# Revit family: 9144944
name_source: partatom
category: Lighting Fixtures
revit_build: Autodesk Revit 2017 (Build: 20190507_1515(x64)
units: mm (PartAtom-declared; Revit-internal decimal feet)

## family parameters
Cut with Voids When Loaded = No
Host = Face
Light Source = Yes
OmniClass Number = 23.80.70.00
OmniClass Title = Lighting
Part Type = Normal
Room Calculation Point = No
Round Connector Dimension = Use Diameter
Shared = No

## types (2) — shared parameters
Apparent Load = 7 VA
Assembly Code = D5020200
AssetType = Fixed
ClassificationName = Uniclass2015
ClassificationValue = EF_70_80
Color Filter = 16777215
Default Elevation = 1219 mm
Dimming Lamp Color Temperature Shift = <None>
DimmingControlOptions = Non dimmable
DocumentationLiterature = http://www.sylvania-lighting.com
DurationUnit = hours
ElectricShockClassification = Class II
Emit Shape Visible in Rendering = No
Emit from Rectangle Length = 305 mm  [stored 1.00066 ft]
Emit from Rectangle Width = 40 mm  [stored 0.131234 ft]
ExpectedLife = 50000
IfcExportAs = IfcLightFixtureType
IfcExportType = IfcLightFixtureType
IngressProtection = IP65
InputNominalFrequency = 50/60 Hz
InputVoltage = 230-240V~
Keynote = 16500
Lamp = LED
LampColourTemperature = 4000 K
LampNominalLuminous = 135 lm
LampsType = LED
LuminousEfficacy = 46.53 lm/W
Manufacturer = Feilo Sylvania
ManufacturerName = Feilo Sylvania
Material_1_SYL = PC/ABS Plastic
Material_2_SYL = PC/ABS Plastic Transparent
Material_3_SYL = LED-Sylvania
Material_4_SYL = EM sign
Model = SYLSAFE IP65 LED M3
ModelNumber = 9144944
ModelReference = SYLSAFE IP65 LED M3
Name = SYLSAFE IP65 LED M3
NominalDepth = 110 mm  [stored 0.360892 ft]
NominalHeight = 60 mm  [stored 0.19685 ft]
NominalLength = 346 mm  [stored 1.13517 ft]
Photometric Web File = 9144944.ies
PowerConsumption = 7 W
Tilt Angle = -90.00°
Type Image = <None>
TypeName = SYLSAFE IP65 LED M3
URL = http://www.sylvania-lighting.com
Voltage = 230 V
Weight = 2.75 kg
zero-valued in all types: Cost, PowerFactor

## per-type parameters (varying)
| type | Cover_SYL | EmergencyAccessory_SYL |
| 9144944 SYLSAFE IP65 LED M3 | Yes | No |
| 9144944 SYLSAFE IP65 LED M3 Emergency mode | No | Yes |

note: [stored X ft] marks values corroborated as IEEE doubles in the binary element streams (Revit-internal decimal feet)

## geometry (parser evidence)
native form markers: Sweep x4
no freeform markers — native parametric forms only
